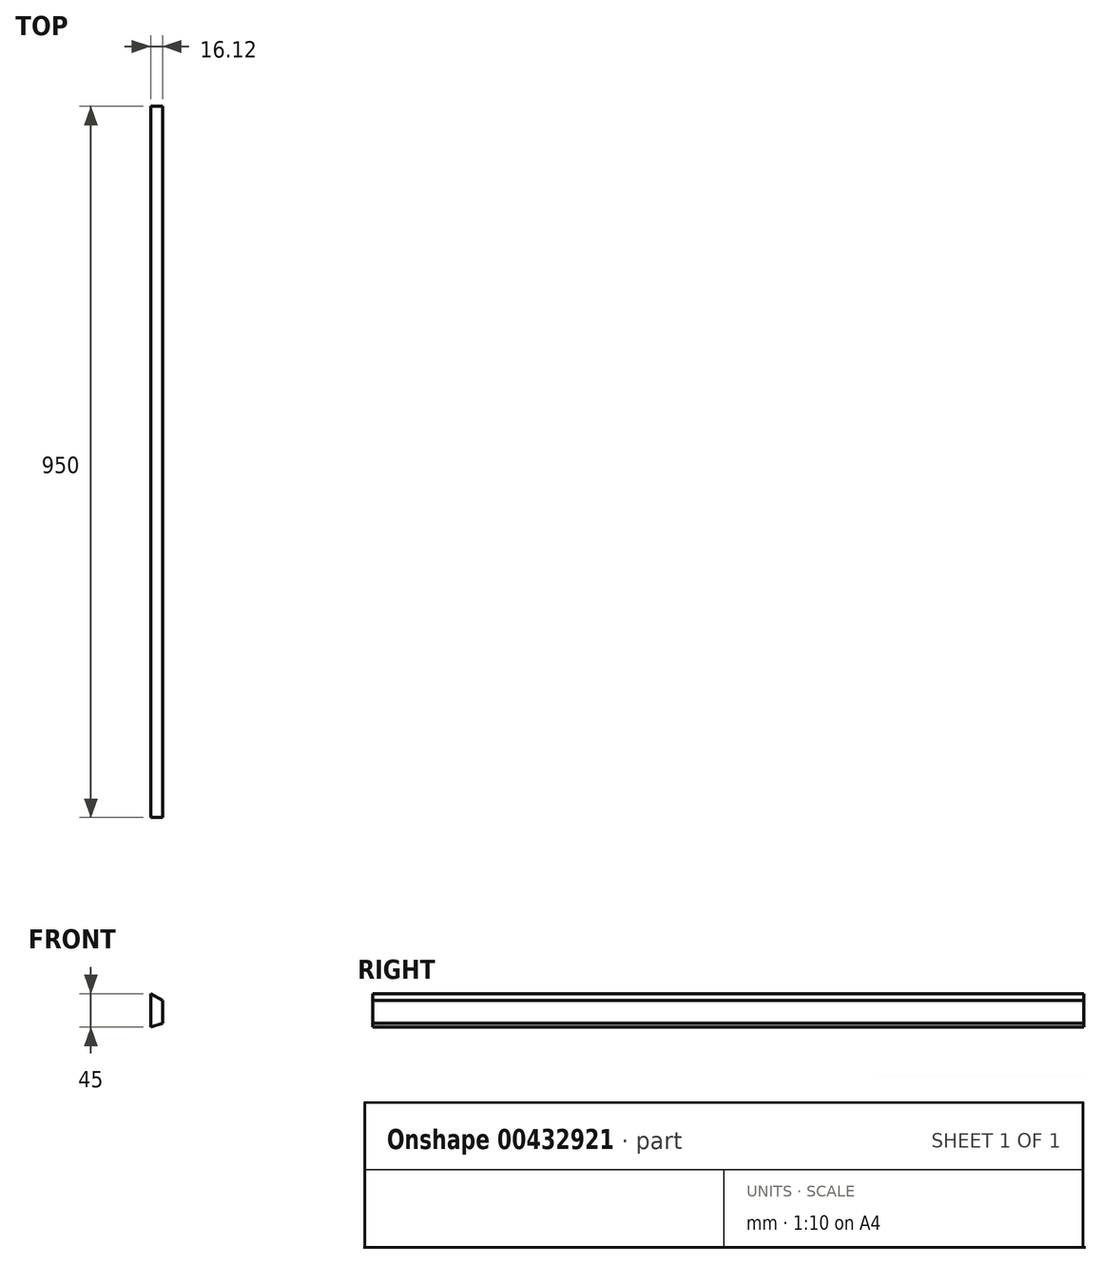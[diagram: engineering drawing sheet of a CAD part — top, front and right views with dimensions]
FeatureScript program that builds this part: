
annotation { "Feature Type Name" : "Feature", "Feature Type Description" : "" }
export const myFeature = defineFeature(function(context is Context, id is Id, definition is map)
    precondition{}
    {
        {
            var Q0;
            Q0=qCreatedBy(makeId("Front.planeOp"),FACE);
            var sketch = newSketch(context, id + "F0", { "sketchPlane" : qUnion([Q0])});
            skLineSegment(sketch, "E0", {"start": v(-8.06, 23.5) * mm, "end": v(-8.06, -21.5) * mm});
            skLineSegment(sketch, "E1", {"start": v(-8.06, -21.5) * mm, "end": v(8.06, -16) * mm});
            skLineSegment(sketch, "E2", {"start": v(8.06, -16) * mm, "end": v(8.06, 14) * mm});
            skLineSegment(sketch, "E3", {"start": v(8.06, 14) * mm, "end": v(-8.06, 23.5) * mm});
            skSolve(sketch);
        }
        {
            var Q0;
            Q0 = qSketchRegion(id + "F0", true);
            extrude(context, id + "F1", {"entities" : qUnion([Q0]), "depth" : 950 * mm});
        }
    });
